# Revit family: QF_RANCILIO_EGRO ONE TOUCH PURE COFFEE WITH POWDER
name_source: partatom
category: Specialty Equipment
revit_build: Autodesk Revit 2014 (Build: 20130308_1515(x64)
units: mm (PartAtom-declared; Revit-internal decimal feet)

## types (1)
- ONE TOUCH PURE COFFEE WITH POWDER
    Apparent Power = 0 VA
    Cold Water Connection Height = 0 mm  [stored 0 ft]
    Cold Water Flow = 0 GPM
    Cold Water Maximum Pressure = 0.00 psi
    Cold Water Minimum Pressure = 0.00 psi
    Cold Water RI Height = 0 mm  [stored 0 ft]
    Cold Water Size = 0"
    Cold Water Temperature Recommended = -460 °F
    Conn Conduit = Yes
    Conn Plug = Typ 25 / CEE
    Cycle = 50 Hz
    Depth = 584.2 mm  [stored 1.91667 ft]
    Description = ESPRESSO MACHINE
    Elec Conn Connection Height = 0 mm  [stored 0 ft]
    Elec Conn RI Height = 0 mm  [stored 0 ft]
    FL Amps = 16 A
    Foodservice Equipment Identifier = Yes
    Height = 787.4 mm
    Identify Quantity as Lot = Yes
    Indirect Waste Connection Height = 0 mm  [stored 0 ft]
    Indirect Waste Flow = 0 GPM
    Indirect Waste Size = 2"
    Length = 300.99 mm  [stored 0.9875 ft]
    Manufacturer = RANCILIO
    Max Overcurrent Protection = 0 A
    Min Ckt Ampacity = 0 A
    Model = ONE TOUCH PURE COFFEE WITH POWDER
    Model Visibility = 4
    Number of Poles = 1
    Phase = 2
    Top Milk XP NMS Powder = Yes
    Touch Quick Milk NMS = No
    Touch Top Milk  XP NMS = No
    Volts = 400 V
    Watts = 6000 W
    Weight in Kilograms = 70

note: [stored X ft] marks values corroborated as IEEE doubles in the binary element streams (Revit-internal decimal feet)

## geometry (parser evidence)
native form markers: Sweep x5
no freeform markers — native parametric forms only
